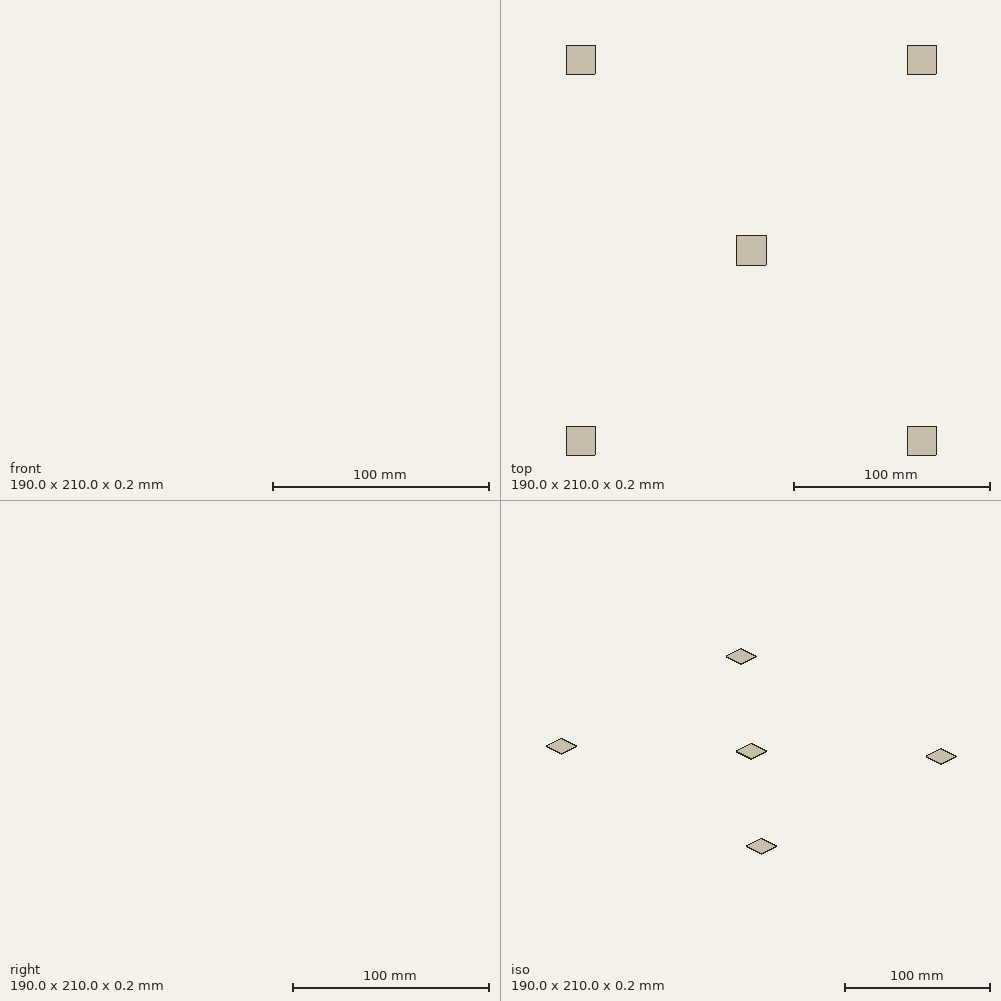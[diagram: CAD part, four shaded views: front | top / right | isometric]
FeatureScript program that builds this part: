
annotation { "Feature Type Name" : "Feature", "Feature Type Description" : "" }
export const myFeature = defineFeature(function(context is Context, id is Id, definition is map)
    precondition{}
    {
        {
            var Q0;
            Q0=qCreatedBy(makeId("Top.planeOp"),FACE);
            var sketch = newSketch(context, id + "F0", { "sketchPlane" : qUnion([Q0])});
            skLineSegment(sketch, "E0.bottom", {"start": v(100, 125) * mm, "end": v(-100, 125) * mm});
            skLineSegment(sketch, "E0.top", {"start": v(100, -125) * mm, "end": v(-100, -125) * mm});
            skLineSegment(sketch, "E0.left", {"start": v(100, 125) * mm, "end": v(100, -125) * mm});
            skLineSegment(sketch, "E0.right", {"start": v(-100, 125) * mm, "end": v(-100, -125) * mm});
            skPoint(sketch, "E0.middle", {"position": v(0, 0) * mm});
            skSolve(sketch);
        }
        {
            var Q0;
            Q0=qCreatedBy(makeId("Top.planeOp"),FACE);
            var sketch = newSketch(context, id + "F1", { "sketchPlane" : qUnion([Q0])});
            skLineSegment(sketch, "E1.bottom", {"start": v(-100, 125) * mm, "end": v(100, 125) * mm, "construction": true});
            skLineSegment(sketch, "E1.top", {"start": v(-100, -125) * mm, "end": v(100, -125) * mm, "construction": true});
            skLineSegment(sketch, "E1.left", {"start": v(-100, 125) * mm, "end": v(-100, -125) * mm, "construction": true});
            skLineSegment(sketch, "E1.right", {"start": v(100, 125) * mm, "end": v(100, -125) * mm, "construction": true});
            skPoint(sketch, "E1.middle", {"position": v(0, 0) * mm});
            skLineSegment(sketch, "E2", {"start": v(0, 125) * mm, "end": v(0, 0) * mm, "construction": true});
            skLineSegment(sketch, "E3", {"start": v(0, 0) * mm, "end": v(100, 0) * mm, "construction": true});
            skLineSegment(sketch, "E4.bottom", {"start": v(-95, 105) * mm, "end": v(-80, 105) * mm});
            skLineSegment(sketch, "E4.top", {"start": v(-95, 90) * mm, "end": v(-80, 90) * mm});
            skLineSegment(sketch, "E4.left", {"start": v(-95, 105) * mm, "end": v(-95, 90) * mm});
            skLineSegment(sketch, "E4.right", {"start": v(-80, 105) * mm, "end": v(-80, 90) * mm});
            skLineSegment(sketch, "E5.MirrorCS", {"start": v(95, 105) * mm, "end": v(80, 105) * mm});
            skLineSegment(sketch, "E6.MirrorCS", {"start": v(95, 90) * mm, "end": v(80, 90) * mm});
            skLineSegment(sketch, "E7.MirrorCS", {"start": v(80, 105) * mm, "end": v(80, 90) * mm});
            skLineSegment(sketch, "E8.MirrorCS", {"start": v(95, 105) * mm, "end": v(95, 90) * mm});
            skLineSegment(sketch, "E9.MirrorCS", {"start": v(80, -105) * mm, "end": v(80, -90) * mm});
            skLineSegment(sketch, "E10.MirrorCS", {"start": v(95, -90) * mm, "end": v(80, -90) * mm});
            skLineSegment(sketch, "E11.MirrorCS", {"start": v(95, -105) * mm, "end": v(80, -105) * mm});
            skLineSegment(sketch, "E12.MirrorCS", {"start": v(-95, -105) * mm, "end": v(-95, -90) * mm});
            skLineSegment(sketch, "E13.MirrorCS", {"start": v(-95, -105) * mm, "end": v(-80, -105) * mm});
            skLineSegment(sketch, "E14.MirrorCS", {"start": v(95, -105) * mm, "end": v(95, -90) * mm});
            skLineSegment(sketch, "E15.MirrorCS", {"start": v(-95, -90) * mm, "end": v(-80, -90) * mm});
            skLineSegment(sketch, "E16.MirrorCS", {"start": v(-80, -105) * mm, "end": v(-80, -90) * mm});
            skLineSegment(sketch, "E17.bottom", {"start": v(7.5, 7.5) * mm, "end": v(-7.5, 7.5) * mm});
            skLineSegment(sketch, "E17.top", {"start": v(7.5, -7.5) * mm, "end": v(-7.5, -7.5) * mm});
            skLineSegment(sketch, "E17.left", {"start": v(7.5, 7.5) * mm, "end": v(7.5, -7.5) * mm});
            skLineSegment(sketch, "E17.right", {"start": v(-7.5, 7.5) * mm, "end": v(-7.5, -7.5) * mm});
            skSolve(sketch);
        }
        {
            var Q0;
            Q0 = qSketchRegion(id + "F1", true);
            extrude(context, id + "F2", {"entities" : qUnion([Q0]), "depth" : 0.2 * mm, "offsetDistance" : 25 * mm});
        }
    });
